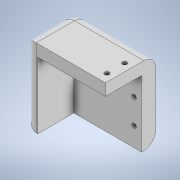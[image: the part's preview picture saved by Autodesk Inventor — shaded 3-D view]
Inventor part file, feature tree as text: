
AUTODESK INVENTOR PART (.ipt)
format: ipt  version: 2021 (Build 250183000, 183)  size: 142,336 bytes
history: native  units: mm
features: extrude x3, sketch x3, other x1, fillet x1
ambient origin geometry x8: Origin, YZ Plane, XZ Plane, XY Plane, X Axis, Y Axis, Z Axis, Center Point
bodies: Body1 (feature_tree)
feature tree (8):
  other  "Sólido1"
  extrude  "Extrusión1"  Depth=10.0mm
  extrude  "Extrusión2"  Depth=8.0mm TaperAngle=0.0deg
  extrude  "Extrusión3"  Depth=9.0mm
  fillet  "Empalme1"  Radius=45.0mm
  sketch  "Boceto1"  dims[d0=24.0mm d4=10.0mm]
  sketch  "Boceto2"  dims[d7=5.0mm d11=8.0mm d12=0.0mm]
  sketch  "Boceto3"  dims[d15=24.5mm d16=9.0mm d17=45.0mm d18=0.0mm d24=45.0mm d25=0.0mm d26=8.0mm d19=0.5mm d20=0.872665mm]
